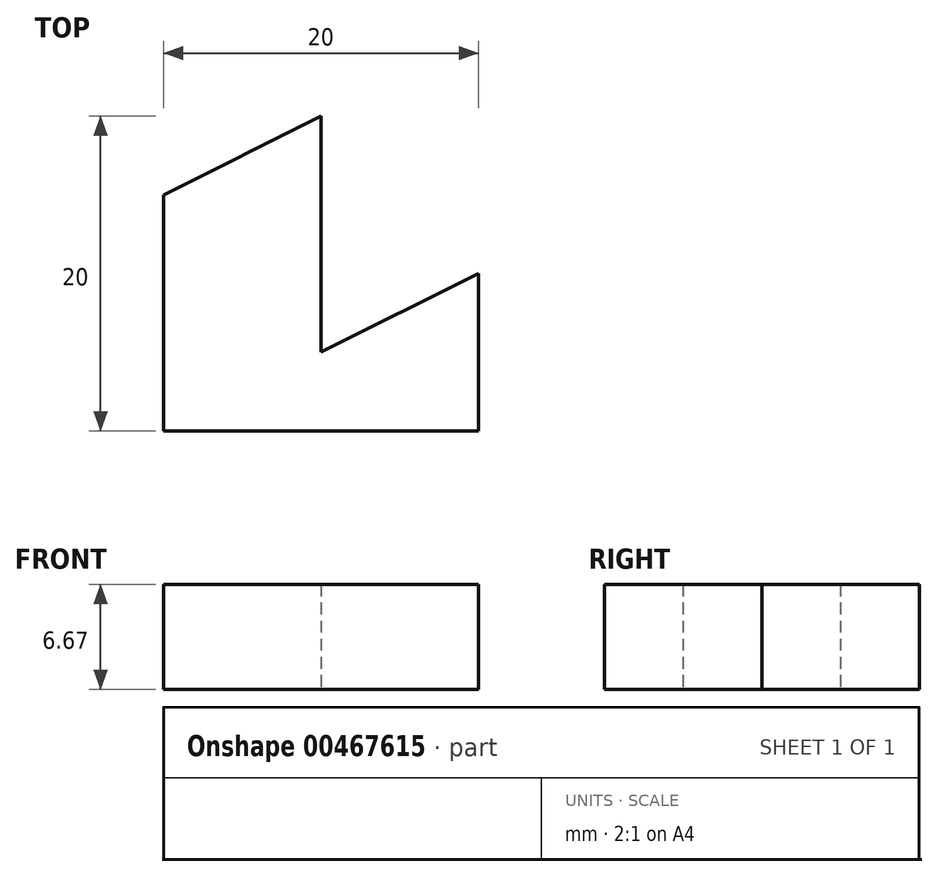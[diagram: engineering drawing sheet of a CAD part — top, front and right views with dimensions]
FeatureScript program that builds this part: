
annotation { "Feature Type Name" : "Feature", "Feature Type Description" : "" }
export const myFeature = defineFeature(function(context is Context, id is Id, definition is map)
    precondition{}
    {
        {
            var Q0;
            Q0=qCreatedBy(makeId("Top.planeOp"),FACE);
            var sketch = newSketch(context, id + "F0", { "sketchPlane" : qUnion([Q0])});
            skLineSegment(sketch, "E0", {"start": v(-35.56, -15.94) * mm, "end": v(-35.56, -30.94) * mm});
            skLineSegment(sketch, "E1", {"start": v(-45.56, -35.94) * mm, "end": v(-25.56, -35.94) * mm});
            skLineSegment(sketch, "E2", {"start": v(-45.56, -35.94) * mm, "end": v(-45.56, -20.94) * mm});
            skLineSegment(sketch, "E3", {"start": v(-45.56, -20.94) * mm, "end": v(-35.56, -15.94) * mm});
            skLineSegment(sketch, "E4", {"start": v(-25.56, -35.94) * mm, "end": v(-25.56, -25.94) * mm});
            skLineSegment(sketch, "E5", {"start": v(-25.56, -25.94) * mm, "end": v(-35.56, -30.94) * mm});
            skSolve(sketch);
        }
        {
            var Q0;
            Q0=makeQuery(id+"F0.imprint","IMPRINT",FACE,{"disambiguationData":[TD([[makeQuery(id+"F0.imprint","IMPRINT",EDGE,{"derivedFrom":sQuery(id+"F0.wireOp",EDGE,"E0")}),-1.0]])]});
            extrude(context, id + "F1", {"entities" : qUnion([Q0]), "depth" : 6.67 * mm});
        }
    });
